# Revit family: AUU-1018-14
name_source: partatom
category: Plumbing Fixtures
revit_build: Autodesk Revit 2018 (Build: 20170223_1515(x64)
units: mm (PartAtom-declared; Revit-internal decimal feet)

## family parameters
Always vertical = No
Cut with Voids When Loaded = No
OmniClass Number = 23.45.05.14.99
OmniClass Title = Other Sanitary Washing Plumbing Fixtures
Part Type = Normal
Room Calculation Point = No
Round Connector Dimension = Use Radius
Shared = Yes
Work Plane-Based = Yes

## types (3) — shared parameters
ADA Compliant = Yes
Assembly Code = D2020300
Buy American Act Compliant = Yes
CW Connection = Yes
CWFU = 10
Default Elevation = 0"
Description = Exposed Water Closet Flushometer for floor mounted or wall hung top spud bowls.
Finish(es) = CP, PVDSF, PVDPB, PVDBN
Fixture Color = Not Applicable
Flush Choice = Single Flush
HW Connection = No
IAPMO Certification = cUPC
Inlet Spud Radius = 1/2"
Inlet Spud Size = 1" IPS
Manufacturer = SLOAN
Mounting = Exposed
Operation = Manual
Price = Prices may vary. Please consult Sloan Rep for most up-to-date price list.
Product Page URL = http://www.sloanvalve.com
Revision Date = 12/6/2015
Rough In = 11-1/2"
Spud Location = Top Spud
URL = www.sloanvalve.com
Vent Connection = No
WFU = 10
Warranty = 3 Year (Limited)
Waste Connection = No
zero-valued in all types: HWFU

## per-type parameters (varying)
| type | Flush Volume | Model |
| Sloan 111-1.28 | 1.28 gpf (4.8 Lpf) | Royal 111-1.28 |
| Sloan 111-1.6 | 1.6 gpf (6.0 Lpf) | Royal 111-1.6 |
| Sloan 110- 3.5 | 3.5 gpf (13.2 Lpf) | Royal 111-1.6 |

## geometry (parser evidence)
native form markers: Sweep x2
no freeform markers — native parametric forms only
